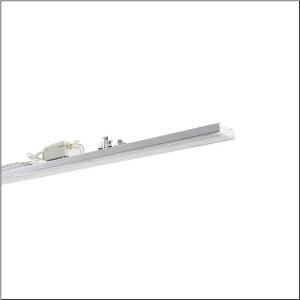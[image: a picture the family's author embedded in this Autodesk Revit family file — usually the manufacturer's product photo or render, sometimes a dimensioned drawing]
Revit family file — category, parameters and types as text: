
# Revit family: licross_21_recessed_mo_52tl11dv4fxg
name_source: partatom
category: Lighting Fixtures
units: mm (PartAtom-declared; Revit-internal decimal feet)

## family parameters
Cut with Voids When Loaded = No
Host = Face
Light Source = No
Part Type = Normal
Room Calculation Point = No
Round Connector Dimension = Use Diameter
Shared = No

## types (1)
- --- (1 x LED, 15180 lm, 85.3 W, 4000K)
    Apparent Load = 85 VA
    CIE Flux Codes = 89 96 99 100 100
    Color Rendering = 80
    Color Temperature = 4000K
    Default Elevation = 1800 mm
    Description = Licross 21 Recessed MO, luminaire insert, of sheet steel, galvanised, coil coated, white, length: 2.250mm, width: 66mm, height: 67mm, LED rated luminous flux: 15.180lm, light colour: 840, SDCM (Standard Deviation of Colour Matching)MacAdam ≤ 3 SDCM (initial), control gear: DALI 2, with plug, 5-pole, with phase selection, mains connection: 220..240V, AC, 50/60Hz, rated input power: 85W, internal wiring halogen-free, primary light control with lens, of plastic, primary optical cover: cover, of PMMA, light emission: direct distribution, primary light characteristic: symmetric, protection rating (complete): IP40, insulation class (complete): insulation class I (protective earthing), certification: CE, ENEC, VDE, UKCA, protection symbol: D if used in an environment without relevant dust loads with corresponding accessories, impact resistance: IK06, permissible ambient temperature for indoor applications: -25..+35°C, corresponds to IFS (International Featured Standards) requirements for safety and quality in the food industry, reducing of maximum allowable ambient temperature of 5°C with ceiling mounting, LABS conformity tested according to VDMA 24364:2018-05, The light source and the operating device comply with the requirements of the Ecodesign Regulation (EU) 2019/2020 and are replaceable in accordance with this regulation, packaging unit: 1 piece
    Height = 58 mm
    Lamp = 1 x LED
    Lamp Light Flux = 15180 lm
    Lamp Power = 85.3 W
    Lamp count = 1
    Length = 2250 mm
    Luminous efficacy = 178 lm/W
    Manufacturer = Siteco
    ModVariant = No
    Model = 52TL11DV4FXG
    Mounting Place = Ceiling
    Mounting Type = Pendant
    Number of Poles = 1
    OnlyDefault = Yes
    Power Factor = 1
    Product Name = Licross 21 Recessed MO
    Product group = luminaire insert | ceiling pendant
    ProductGroupID = 901
    Protection Class = Protection class I
    Protection Degree = IP 40
    RLX_Detail_Level = 1
    RLX_Emergency_Light_Flux = 0 lm
    RLX_Emergency_Type = 0
    RLX_Emergency_Type_DB = No
    RlxData = <blob elided: 29865 chars, md5=e611ac7c>
    Socket = socket
    Standby Power = 0 W
    System Light Flux = 15180 lm
    System Power = 85 W
    Type Comments = factory setting: luminous flux: 100 % | dim-lin: 254 | 390 mA
    Type Image = l_1296930.jpg
    URL = http://relux.com
    VarID = @adj_128815
    Voltage = 0 V
    Weight = 0.00 kg
    Width = 66 mm

## geometry (parser evidence)
native form markers: Blend x4, Sweep x9
no freeform markers — native parametric forms only
